# Revit family: Digital_Media-Honeywell-Universal_Interface_Module-583331-21
name_source: partatom
category: Electrical Equipment
revit_build: Autodesk Revit 2017 (Build: 20160225_1515(x64)
units: mm (PartAtom-declared; Revit-internal decimal feet)

## family parameters
Cut with Voids When Loaded = No
Host = Face
OmniClass Number = 23.85.50.00
OmniClass Title = Communication Systems
Part Type = Equipment Switch
Room Calculation Point = No
Round Connector Dimension = Use Diameter
Shared = No

## types (1)
- Universal Interface Module UIM - 583331.21
    Air Humidity = 15 ... 90 %
    Ambient Temperature = -5 °C ... 55 °C
    Apparent Load = 0 VA
    Default Elevation = 1219 mm
    Depth = 345 mm  [stored 1.13189 ft]
    Description = Universal Interface Module UIM
    Finish = Metal - Honeywell - Stainless Steel - Black
    Frequency = 47 Hz
    Height = 44 mm  [stored 0.144357 ft]
    Inputs = max. 36 V DC
    Load Sub-Classification = No
    Manufacturer = Honeywell International
    Manufacturer Fax Number = 02131/40615-606
    Model = 583331.21
    Number of Poles = 1
    Outputs = 36 V DC/50 mA
    Power Factor = 1
    Product Documentation Link = https://www.esser-systems.com
    Product Name = UIM
    Product Page URL = https://www.esser-systems.com
    URL = www.esser-systems.com
    Utility = No
    Version = 2017 - v1.0a
    Voltage = 36 V
    Wattage = 24 W
    Watts = 24 W
    Weight = 3.60 kgf
    Width = 483 mm

note: [stored X ft] marks values corroborated as IEEE doubles in the binary element streams (Revit-internal decimal feet)

## geometry (parser evidence)
native form markers: Sweep x3
no freeform markers — native parametric forms only
